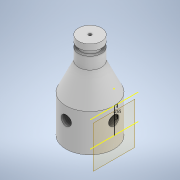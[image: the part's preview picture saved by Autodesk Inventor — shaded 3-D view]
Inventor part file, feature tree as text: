
AUTODESK INVENTOR PART (.ipt)
format: ipt  version: 2020 (Build 240168000, 168)  size: 215,552 bytes
history: native  units: in
note: dims shown in document units (in); Inventor stores cm internally (conversion verified against a paired STEP export)
features: sketch x5, hole x4, revolve x1, plane x1, extrude x1, pattern_circular x1
ambient origin geometry x8: Origin, YZ Plane, XZ Plane, XY Plane, X Axis, Y Axis, Z Axis, Center Point
bodies: Solid1 (feature_tree)
feature tree (13):
  revolve  "Revolution1"  [1 undecoded]
  hole  "Hole4"  [1 undecoded]
  sketch  "Sketch13"  dims[d4=0.095in d5=0.125in]
  plane  "Work Plane1"
  sketch  "Sketch14"  dims[d6=90.0deg d23=0.65in]
  hole  "Hole5"  [1 undecoded]
  hole  "Hole6"  [1 undecoded]
  extrude  "Extrusion3"  Depth=0.125in
  hole  "Hole8"  [1 undecoded]
  pattern_circular  "Circular Pattern5"  [2 undecoded]
  sketch  "Sketch1"  dims[d0=0.239in d1=0.5in]
  sketch  "Sketch12"  dims[d2=90.0deg d3=0.057in]
  sketch  "Sketch16"  dims[d24=0.4466in d25=0.125in d54=0.3779in d72=0.3779in d83=0.5in d84=0.5in d85=0.0625in d86=0.75in d87=0.375in d88=0.25in d89=0.5635in d90=1.294in d91=0.8108in d92=0.2645in d93=0.0625in d94=0.75in d95=0.375in d96=0.25in d97=0.5635in d98=0.5in d99=0.8108in d100=0.211in d101=0.25in d102=0.375in d103=0.25in d104=0.5635in d105=0.25in d106=0.0in d119=0.25in d120=0.0in d121=0.196in d122=0.25in d123=0.375in d124=0.25in d125=0.5635in d126=0.25in d127=0.0in d137=0.3779in d155=0.3779in d173=0.3779in d191=0.3779in d211=1.5748in d212=360.0deg d221=0.3779in d239=0.3779in]
note: 7 required parameter values undecoded (feature->parameter linkage not recoverable at this tier; creation-order binding heuristic only, values carry confidence <= 0.55)